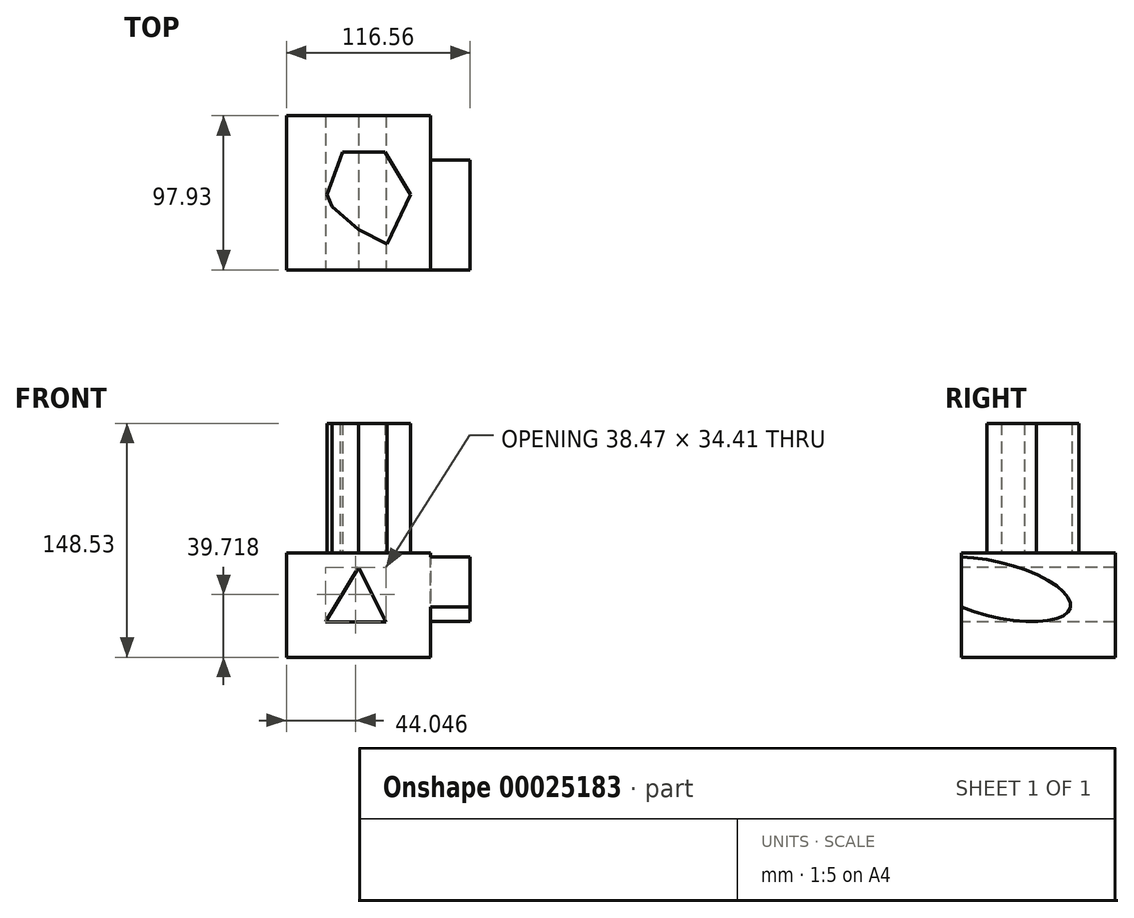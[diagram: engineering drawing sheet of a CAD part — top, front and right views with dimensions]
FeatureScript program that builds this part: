
annotation { "Feature Type Name" : "Feature", "Feature Type Description" : "" }
export const myFeature = defineFeature(function(context is Context, id is Id, definition is map)
    precondition{}
    {
        {
            var Q0;
            Q0=qCreatedBy(makeId("Top.planeOp"),FACE);
            var sketch = newSketch(context, id + "F0", { "sketchPlane" : qUnion([Q0])});
            skLineSegment(sketch, "E0.rect.bottom", {"start": v(-45.78, 50.14) * mm, "end": v(45.78, 50.14) * mm});
            skLineSegment(sketch, "E0.rect.top", {"start": v(-45.78, -47.8) * mm, "end": v(45.78, -47.8) * mm});
            skLineSegment(sketch, "E0.rect.left", {"start": v(-45.78, 50.14) * mm, "end": v(-45.78, -47.8) * mm});
            skLineSegment(sketch, "E0.rect.right", {"start": v(45.78, 50.14) * mm, "end": v(45.78, -47.8) * mm});
            skPoint(sketch, "E0.rect.middle", {"position": v(0, 1.17) * mm});
            skSolve(sketch);
        }
        {
            var Q0;
            Q0=makeQuery(id+"F0.imprint","IMPRINT",FACE,{"disambiguationData":[TD([[makeQuery(id+"F0.imprint","IMPRINT",EDGE,{"derivedFrom":sQuery(id+"F0.wireOp",EDGE,"E0.rect.bottom")}),-1.0]])]});
            extrude(context, id + "F1", {"entities" : qUnion([Q0]), "depth" : 66.37 * mm});
        }
        {
            var Q0;
            Q0=makeQuery(id+"F1.opExtrude","SWEPT_FACE",FACE,{"disambiguationData":[OSD([sQuery(id+"F0.wireOp",EDGE,"E0.rect.top")])]});
            var sketch = newSketch(context, id + "F2", { "sketchPlane" : qUnion([Q0])});
            skSolve(sketch);
        }
        {
            var Q0;
            {var subQ0=sQuery(id+"F0.wireOp",EDGE,"E0.rect.top");Q0=makeQuery(id+"F2.imprint","IMPRINT",FACE,{"disambiguationData":[TD([[makeQuery(id+"F2.imprint","IMPRINT",EDGE,{"derivedFrom":makeQuery(id+"F1.opExtrude","CAP_EDGE",EDGE,{"disambiguationData":[OSD([subQ0])],"isStart":true})}),1.0]])]});}
            var sketch = newSketch(context, id + "F3", { "sketchPlane" : qUnion([Q0])});
            skLineSegment(sketch, "E1", {"start": v(17.5, 22.51) * mm, "end": v(0, 56.93) * mm});
            skLineSegment(sketch, "E2", {"start": v(0, 56.93) * mm, "end": v(-20.97, 22.51) * mm});
            skLineSegment(sketch, "E3", {"start": v(-20.97, 22.51) * mm, "end": v(17.5, 22.51) * mm});
            skSolve(sketch);
        }
        {
            var Q0;
            Q0=makeQuery(id+"F3.imprint","IMPRINT",FACE,{"disambiguationData":[TD([[makeQuery(id+"F3.imprint","IMPRINT",EDGE,{"derivedFrom":sQuery(id+"F3.wireOp",EDGE,"E1")}),1.0]])]});
            extrude(context, id + "F4", {"entities" : qUnion([Q0]), "operationType" : NewBodyOperationType.REMOVE, "oppositeDirection" : true, "depth" : 398.27 * mm});
        }
        {
            var Q0;
            Q0=makeQuery(id+"F1.opExtrude","CAP_FACE",FACE,{"disambiguationData":[OSD([sQuery(id+"F0.wireOp",EDGE,"E0.rect.bottom"),sQuery(id+"F0.wireOp",EDGE,"E0.rect.top"),sQuery(id+"F0.wireOp",EDGE,"E0.rect.left"),sQuery(id+"F0.wireOp",EDGE,"E0.rect.right")])],"isStart":false});
            var sketch = newSketch(context, id + "F5", { "sketchPlane" : qUnion([Q0])});
            skLineSegment(sketch, "E4", {"start": v(32.93, 0) * mm, "end": v(16.73, 26.98) * mm});
            skLineSegment(sketch, "E5", {"start": v(16.73, 26.98) * mm, "end": v(0, 26.98) * mm});
            skLineSegment(sketch, "E6", {"start": v(0, 26.98) * mm, "end": v(-10.28, 26.98) * mm});
            skLineSegment(sketch, "E7", {"start": v(-11.82, 22.5) * mm, "end": v(-19.82, 0) * mm});
            skLineSegment(sketch, "E8", {"start": v(-10.28, 26.98) * mm, "end": v(-11.82, 22.5) * mm});
            skLineSegment(sketch, "E9", {"start": v(-16.76, -7.5) * mm, "end": v(-19.82, 0) * mm});
            skLineSegment(sketch, "E10", {"start": v(-16.76, -7.5) * mm, "end": v(0, -22.32) * mm});
            skLineSegment(sketch, "E11", {"start": v(0, -22.32) * mm, "end": v(18.19, -31.36) * mm});
            skLineSegment(sketch, "E12", {"start": v(18.19, -31.36) * mm, "end": v(32.93, 0) * mm});
            skSolve(sketch);
        }
        {
            var Q0;
            Q0=makeQuery(id+"F5.imprint","IMPRINT",FACE,{"disambiguationData":[TD([[makeQuery(id+"F5.imprint","IMPRINT",EDGE,{"derivedFrom":sQuery(id+"F5.wireOp",EDGE,"E4")}),1.0]])]});
            extrude(context, id + "F6", {"entities" : qUnion([Q0]), "operationType" : NewBodyOperationType.ADD, "depth" : 82.15 * mm});
        }
        {
            var Q0;
            Q0=makeQuery(id+"F1.opExtrude","SWEPT_FACE",FACE,{"disambiguationData":[OSD([sQuery(id+"F0.wireOp",EDGE,"E0.rect.right")])]});
            var sketch = newSketch(context, id + "F7", { "sketchPlane" : qUnion([Q0])});
            skEllipse(sketch, "E13", {"center": v(-26.22, 43.2) * mm, "majorRadius": 49.29 * mm, "minorRadius": 17.37 * mm, "majorAxis": v(0.97, -0.24)});
            skSolve(sketch);
        }
        {
            var Q0;
            {var subQ0=makeQuery(id+"F1.opExtrude","SWEPT_EDGE",EDGE,{"disambiguationData":[OSD([sQuery(id+"F0.wireOp",EDGE,"E0.rect.top"),sQuery(id+"F0.wireOp",EDGE,"E0.rect.right")])]});var subQ1=sQuery(id+"F7.wireOp",EDGE,"E13");var subQ3=makeQuery(id+"F7.imprint","INTERSECT",VERTEX,{"disambiguationData":[OD(0.0)],"derivedFrom":[subQ0,subQ1]});Q0=makeQuery(id+"F7.imprint","IMPRINT",FACE,{"disambiguationData":[TD([[makeQuery(id+"F7.imprint","IMPRINT",EDGE,{"disambiguationData":[TD([[subQ3,-1.0]])],"derivedFrom":subQ1}),1.0]])]});}
            extrude(context, id + "F8", {"entities" : qUnion([Q0]), "operationType" : NewBodyOperationType.ADD, "depth" : 25 * mm});
        }
    });
